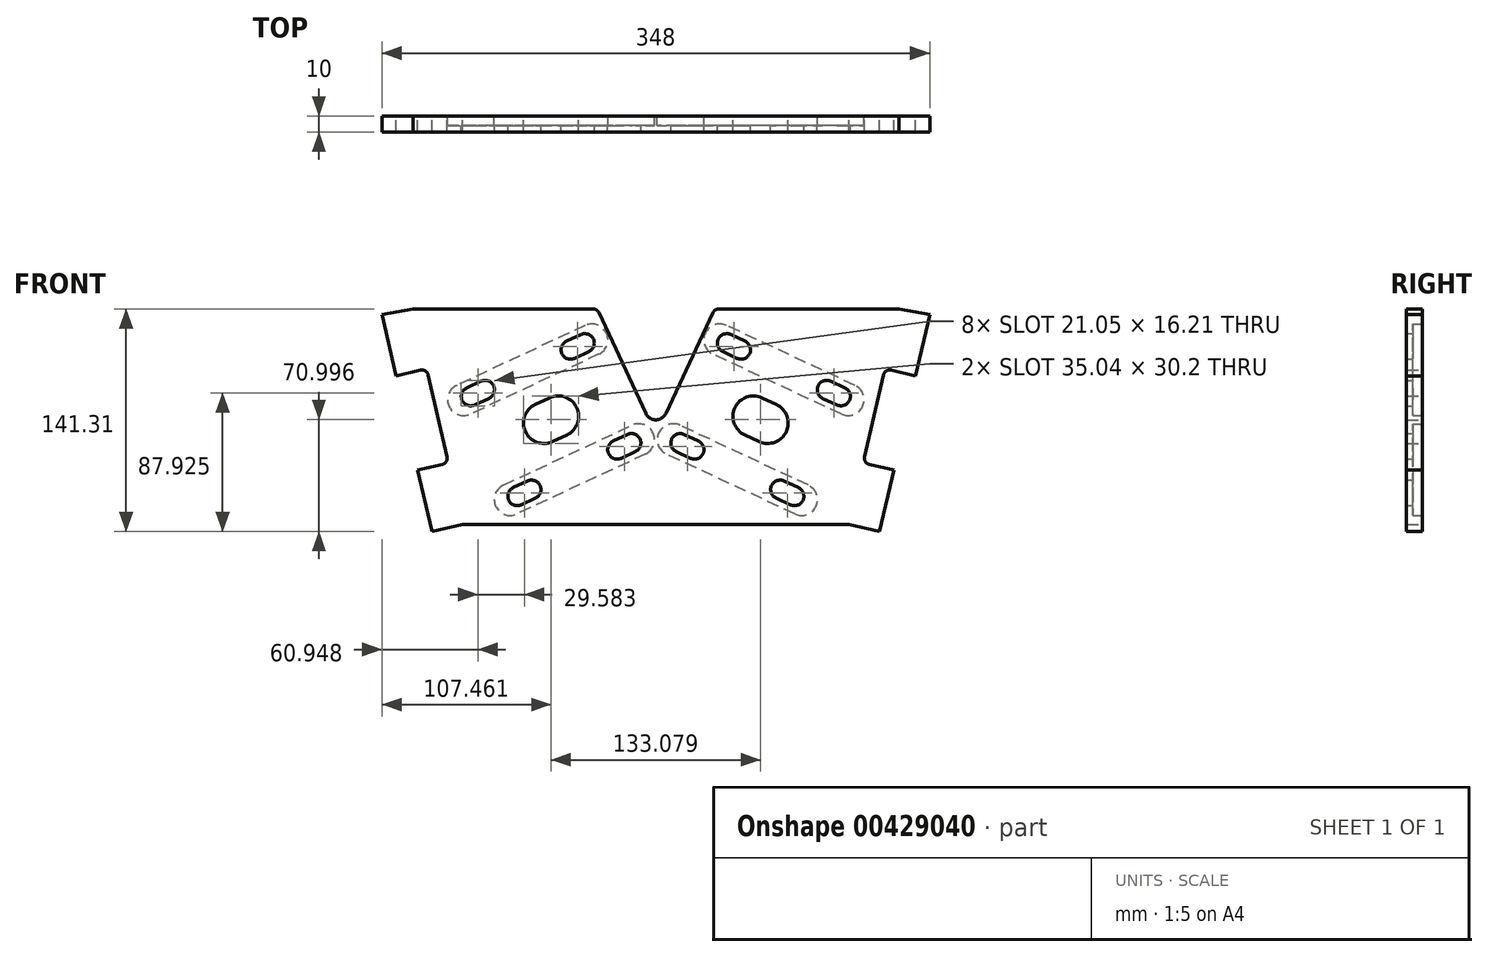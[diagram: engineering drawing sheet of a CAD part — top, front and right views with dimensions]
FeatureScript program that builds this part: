
annotation { "Feature Type Name" : "Feature", "Feature Type Description" : "" }
export const myFeature = defineFeature(function(context is Context, id is Id, definition is map)
    precondition{}
    {
        {
            var Q0;
            Q0=qCreatedBy(makeId("Front.planeOp"),FACE);
            var sketch = newSketch(context, id + "F0", { "sketchPlane" : qUnion([Q0])});
            skLineSegment(sketch, "E0", {"start": v(-39.85, 69.94) * mm, "end": v(-154.27, 69.94) * mm});
            skArc(sketch, "E1", {"start": v(-90.54, -43.56) * mm, "mid": v(-93.44, -51.54) * mm, "end": v(-85.46, -54.44) * mm});
            skArc(sketch, "E2", {"start": v(-76.4, -50.21) * mm, "mid": v(-73.5, -42.24) * mm, "end": v(-81.47, -39.34) * mm});
            skLineSegment(sketch, "E3", {"start": v(-90.54, -43.56) * mm, "end": v(-81.47, -39.34) * mm});
            skLineSegment(sketch, "E4", {"start": v(-85.46, -54.44) * mm, "end": v(-76.4, -50.21) * mm});
            skArc(sketch, "E5.MirrorCS", {"start": v(-22.02, -24.85) * mm, "mid": v(-30, -21.95) * mm, "end": v(-27.1, -13.98) * mm});
            skLineSegment(sketch, "E6.MirrorCS", {"start": v(-12.96, -20.63) * mm, "end": v(-22.02, -24.85) * mm});
            skLineSegment(sketch, "E7.MirrorCS", {"start": v(-18.03, -9.75) * mm, "end": v(-27.1, -13.98) * mm});
            skArc(sketch, "E8.MirrorCS", {"start": v(-18.03, -9.75) * mm, "mid": v(-10.06, -12.65) * mm, "end": v(-12.96, -20.63) * mm});
            skLineSegment(sketch, "E9", {"start": v(-92.27, -39.85) * mm, "end": v(-19.76, -6.04) * mm});
            skLineSegment(sketch, "E10", {"start": v(-83.73, -58.15) * mm, "end": v(-11.23, -24.34) * mm});
            skArc(sketch, "E11", {"start": v(-6.7, -22.23) * mm, "mid": v(-1.81, -8.8) * mm, "end": v(-15.23, -3.92) * mm});
            skLineSegment(sketch, "E12", {"start": v(-19.76, -6.04) * mm, "end": v(-15.23, -3.92) * mm});
            skLineSegment(sketch, "E13", {"start": v(-11.23, -24.34) * mm, "end": v(-6.7, -22.23) * mm});
            skArc(sketch, "E14.MirrorCS", {"start": v(-88.26, -60.27) * mm, "mid": v(-101.69, -55.38) * mm, "end": v(-96.8, -41.96) * mm});
            skLineSegment(sketch, "E15.MirrorCS", {"start": v(-92.27, -39.85) * mm, "end": v(-96.8, -41.96) * mm});
            skLineSegment(sketch, "E16.MirrorCS", {"start": v(-83.73, -58.15) * mm, "end": v(-88.26, -60.27) * mm});
            skLineSegment(sketch, "E17.MirrorCS", {"start": v(-113.31, 5.29) * mm, "end": v(-40.81, 39.1) * mm});
            skLineSegment(sketch, "E18.MirrorCS", {"start": v(-121.85, 23.6) * mm, "end": v(-49.35, 57.4) * mm});
            skArc(sketch, "E19.MirrorCS", {"start": v(-126.38, 21.48) * mm, "mid": v(-131.27, 8.06) * mm, "end": v(-117.85, 3.17) * mm});
            skLineSegment(sketch, "E20.MirrorCS", {"start": v(-113.31, 5.29) * mm, "end": v(-117.85, 3.17) * mm});
            skLineSegment(sketch, "E21.MirrorCS", {"start": v(-121.85, 23.6) * mm, "end": v(-126.38, 21.48) * mm});
            skLineSegment(sketch, "E22.MirrorCS", {"start": v(-40.81, 39.1) * mm, "end": v(-36.28, 41.21) * mm});
            skLineSegment(sketch, "E23.MirrorCS", {"start": v(-49.35, 57.4) * mm, "end": v(-44.82, 59.52) * mm});
            skArc(sketch, "E24.MirrorCS", {"start": v(-44.82, 59.52) * mm, "mid": v(-31.4, 54.63) * mm, "end": v(-36.28, 41.21) * mm});
            skLineSegment(sketch, "E25.MirrorCS", {"start": v(-115.05, 9) * mm, "end": v(-105.98, 13.23) * mm});
            skArc(sketch, "E26.MirrorCS", {"start": v(-111.06, 24.1) * mm, "mid": v(-103.08, 21.2) * mm, "end": v(-105.98, 13.23) * mm});
            skLineSegment(sketch, "E27.MirrorCS", {"start": v(-120.12, 19.88) * mm, "end": v(-111.06, 24.1) * mm});
            skArc(sketch, "E28.MirrorCS", {"start": v(-115.05, 9) * mm, "mid": v(-123.02, 11.9) * mm, "end": v(-120.12, 19.88) * mm});
            skArc(sketch, "E29.MirrorCS", {"start": v(-42.54, 42.81) * mm, "mid": v(-39.64, 50.79) * mm, "end": v(-47.61, 53.69) * mm});
            skLineSegment(sketch, "E30.MirrorCS", {"start": v(-47.61, 53.69) * mm, "end": v(-56.68, 49.46) * mm});
            skLineSegment(sketch, "E31.MirrorCS", {"start": v(-42.54, 42.81) * mm, "end": v(-51.6, 38.59) * mm});
            skArc(sketch, "E32.MirrorCS", {"start": v(-56.68, 49.46) * mm, "mid": v(-59.58, 41.49) * mm, "end": v(-51.6, 38.59) * mm});
            skArc(sketch, "E33", {"start": v(-76.56, 9.3) * mm, "mid": v(-82.85, -7.98) * mm, "end": v(-65.58, -14.27) * mm});
            skLineSegment(sketch, "E34", {"start": v(-76.56, 9.3) * mm, "end": v(-67.5, 13.52) * mm});
            skLineSegment(sketch, "E35", {"start": v(-65.58, -14.27) * mm, "end": v(-56.51, -10.04) * mm});
            skArc(sketch, "E36.trimOffspring", {"start": v(-56.51, -10.04) * mm, "mid": v(-50.23, 7.23) * mm, "end": v(-67.5, 13.52) * mm});
            skLineSegment(sketch, "E37", {"start": v(-174, 66.5) * mm, "end": v(-165, 27.53) * mm});
            skLineSegment(sketch, "E38", {"start": v(-144.61, 28.13) * mm, "end": v(-132.58, -24) * mm});
            skLineSegment(sketch, "E39", {"start": v(-154.27, 69.94) * mm, "end": v(-174, 66.5) * mm});
            skLineSegment(sketch, "E40", {"start": v(-165, 27.53) * mm, "end": v(-149.41, 31.13) * mm});
            skLineSegment(sketch, "E41", {"start": v(-151.17, -32.4) * mm, "end": v(-135.58, -28.8) * mm});
            skLineSegment(sketch, "E42", {"start": v(-142.17, -71.37) * mm, "end": v(-122.68, -66.87) * mm});
            skLineSegment(sketch, "E43.trimOffspring", {"start": v(-151.17, -32.4) * mm, "end": v(-142.17, -71.37) * mm});
            skLineSegment(sketch, "E44.MirrorCS", {"start": v(47.61, 53.69) * mm, "end": v(56.68, 49.46) * mm});
            skLineSegment(sketch, "E45.MirrorCS", {"start": v(83.73, -58.15) * mm, "end": v(88.26, -60.27) * mm});
            skLineSegment(sketch, "E46.MirrorCS", {"start": v(42.54, 42.81) * mm, "end": v(51.6, 38.59) * mm});
            skLineSegment(sketch, "E47.MirrorCS", {"start": v(121.85, 23.6) * mm, "end": v(126.38, 21.48) * mm});
            skLineSegment(sketch, "E48.MirrorCS", {"start": v(18.03, -9.75) * mm, "end": v(27.1, -13.98) * mm});
            skLineSegment(sketch, "E49.MirrorCS", {"start": v(113.31, 5.29) * mm, "end": v(117.85, 3.17) * mm});
            skLineSegment(sketch, "E50.MirrorCS", {"start": v(65.58, -14.27) * mm, "end": v(56.51, -10.04) * mm});
            skLineSegment(sketch, "E51.MirrorCS", {"start": v(85.46, -54.44) * mm, "end": v(76.4, -50.21) * mm});
            skLineSegment(sketch, "E52.MirrorCS", {"start": v(115.05, 9) * mm, "end": v(105.98, 13.23) * mm});
            skLineSegment(sketch, "E53.MirrorCS", {"start": v(12.96, -20.63) * mm, "end": v(22.02, -24.85) * mm});
            skLineSegment(sketch, "E54.MirrorCS", {"start": v(40.81, 39.1) * mm, "end": v(36.28, 41.21) * mm});
            skLineSegment(sketch, "E55.MirrorCS", {"start": v(11.23, -24.34) * mm, "end": v(6.7, -22.23) * mm});
            skLineSegment(sketch, "E56.MirrorCS", {"start": v(120.12, 19.88) * mm, "end": v(111.06, 24.1) * mm});
            skLineSegment(sketch, "E57.MirrorCS", {"start": v(76.56, 9.3) * mm, "end": v(67.5, 13.52) * mm});
            skLineSegment(sketch, "E58.MirrorCS", {"start": v(49.35, 57.4) * mm, "end": v(44.82, 59.52) * mm});
            skLineSegment(sketch, "E59.MirrorCS", {"start": v(90.54, -43.56) * mm, "end": v(81.47, -39.34) * mm});
            skLineSegment(sketch, "E60.MirrorCS", {"start": v(19.76, -6.04) * mm, "end": v(15.23, -3.92) * mm});
            skLineSegment(sketch, "E61.MirrorCS", {"start": v(92.27, -39.85) * mm, "end": v(96.8, -41.96) * mm});
            skArc(sketch, "E62.MirrorCS", {"start": v(42.54, 42.81) * mm, "mid": v(39.64, 50.79) * mm, "end": v(47.61, 53.69) * mm});
            skArc(sketch, "E63.MirrorCS", {"start": v(18.03, -9.75) * mm, "mid": v(10.06, -12.65) * mm, "end": v(12.96, -20.63) * mm});
            skLineSegment(sketch, "E64.MirrorCS", {"start": v(39.85, 69.94) * mm, "end": v(154.27, 69.94) * mm});
            skArc(sketch, "E65.MirrorCS", {"start": v(115.05, 9) * mm, "mid": v(123.02, 11.9) * mm, "end": v(120.12, 19.88) * mm});
            skArc(sketch, "E66.MirrorCS", {"start": v(90.54, -43.56) * mm, "mid": v(93.44, -51.54) * mm, "end": v(85.46, -54.44) * mm});
            skLineSegment(sketch, "E67.MirrorCS", {"start": v(92.27, -39.85) * mm, "end": v(19.76, -6.04) * mm});
            skArc(sketch, "E68.MirrorCS", {"start": v(44.82, 59.52) * mm, "mid": v(31.4, 54.63) * mm, "end": v(36.28, 41.21) * mm});
            skLineSegment(sketch, "E69.MirrorCS", {"start": v(174, 66.5) * mm, "end": v(165, 27.53) * mm});
            skLineSegment(sketch, "E70.MirrorCS", {"start": v(113.31, 5.29) * mm, "end": v(40.81, 39.1) * mm});
            skLineSegment(sketch, "E71.MirrorCS", {"start": v(83.73, -58.15) * mm, "end": v(11.23, -24.34) * mm});
            skLineSegment(sketch, "E72.MirrorCS", {"start": v(154.27, 69.94) * mm, "end": v(39.85, 69.94) * mm});
            skArc(sketch, "E73.MirrorCS", {"start": v(56.51, -10.04) * mm, "mid": v(50.23, 7.23) * mm, "end": v(67.5, 13.52) * mm});
            skLineSegment(sketch, "E74.MirrorCS", {"start": v(154.27, 69.94) * mm, "end": v(174, 66.5) * mm});
            skArc(sketch, "E75.MirrorCS", {"start": v(56.68, 49.46) * mm, "mid": v(59.58, 41.49) * mm, "end": v(51.6, 38.59) * mm});
            skArc(sketch, "E76.MirrorCS", {"start": v(6.7, -22.23) * mm, "mid": v(1.81, -8.8) * mm, "end": v(15.23, -3.92) * mm});
            skArc(sketch, "E77.MirrorCS", {"start": v(88.26, -60.27) * mm, "mid": v(101.69, -55.38) * mm, "end": v(96.8, -41.96) * mm});
            skArc(sketch, "E78.MirrorCS", {"start": v(22.02, -24.85) * mm, "mid": v(30, -21.95) * mm, "end": v(27.1, -13.98) * mm});
            skArc(sketch, "E79.MirrorCS", {"start": v(111.06, 24.1) * mm, "mid": v(103.08, 21.2) * mm, "end": v(105.98, 13.23) * mm});
            skLineSegment(sketch, "E80.MirrorCS", {"start": v(121.85, 23.6) * mm, "end": v(49.35, 57.4) * mm});
            skLineSegment(sketch, "E81.MirrorCS", {"start": v(144.61, 28.13) * mm, "end": v(132.58, -24) * mm});
            skLineSegment(sketch, "E82.MirrorCS", {"start": v(165, 27.53) * mm, "end": v(149.41, 31.13) * mm});
            skArc(sketch, "E83.MirrorCS", {"start": v(76.56, 9.3) * mm, "mid": v(82.85, -7.98) * mm, "end": v(65.58, -14.27) * mm});
            skLineSegment(sketch, "E84.MirrorCS", {"start": v(142.17, -71.37) * mm, "end": v(122.68, -66.87) * mm});
            skLineSegment(sketch, "E85.MirrorCS", {"start": v(151.17, -32.4) * mm, "end": v(135.58, -28.8) * mm});
            skArc(sketch, "E86.MirrorCS", {"start": v(76.4, -50.21) * mm, "mid": v(73.5, -42.24) * mm, "end": v(81.47, -39.34) * mm});
            skArc(sketch, "E87.MirrorCS", {"start": v(126.38, 21.48) * mm, "mid": v(131.27, 8.06) * mm, "end": v(117.85, 3.17) * mm});
            skLineSegment(sketch, "E88.MirrorCS", {"start": v(151.17, -32.4) * mm, "end": v(142.17, -71.37) * mm});
            skArc(sketch, "E89", {"start": v(-6.34, 3.55) * mm, "mid": v(0, -0.49) * mm, "end": v(6.34, 3.55) * mm});
            skLineSegment(sketch, "E90", {"start": v(6.34, 3.55) * mm, "end": v(36.22, 67.63) * mm});
            skLineSegment(sketch, "E91.MirrorCS", {"start": v(-6.34, 3.55) * mm, "end": v(-36.22, 67.63) * mm});
            skArc(sketch, "E92.filletArc", {"start": v(-36.22, 67.63) * mm, "mid": v(-37.7, 69.31) * mm, "end": v(-39.85, 69.94) * mm});
            skArc(sketch, "E93.filletArc", {"start": v(39.85, 69.94) * mm, "mid": v(37.7, 69.31) * mm, "end": v(36.22, 67.63) * mm});
            skLineSegment(sketch, "E94", {"start": v(-122.68, -66.87) * mm, "end": v(122.68, -66.87) * mm});
            skPoint(sketch, "E95.visualSharp", {"position": v(-145.51, 32.03) * mm});
            skArc(sketch, "E95.filletArc", {"start": v(-144.61, 28.13) * mm, "mid": v(-146.4, 30.62) * mm, "end": v(-149.41, 31.13) * mm});
            skPoint(sketch, "E96.visualSharp", {"position": v(-131.68, -27.9) * mm});
            skArc(sketch, "E96.filletArc", {"start": v(-135.58, -28.8) * mm, "mid": v(-133.09, -27.02) * mm, "end": v(-132.58, -24) * mm});
            skPoint(sketch, "E97.visualSharp", {"position": v(145.51, 32.03) * mm});
            skArc(sketch, "E97.filletArc", {"start": v(149.41, 31.13) * mm, "mid": v(146.4, 30.62) * mm, "end": v(144.61, 28.13) * mm});
            skPoint(sketch, "E98.visualSharp", {"position": v(131.68, -27.9) * mm});
            skArc(sketch, "E98.filletArc", {"start": v(132.58, -24) * mm, "mid": v(133.09, -27.02) * mm, "end": v(135.58, -28.8) * mm});
            skSolve(sketch);
        }
        {
            var Q0;
            Q0 = qSketchRegion(id + "F0", true);
            extrude(context, id + "F1", {"entities" : qUnion([Q0]), "depth" : 10 * mm});
        }
        {
            var Q0;
            Q0=makeQuery(id+"F0.imprint","IMPRINT",FACE,{"disambiguationData":[TD([[makeQuery(id+"F0.imprint","IMPRINT",EDGE,{"derivedFrom":sQuery(id+"F0.wireOp",EDGE,"E17.MirrorCS")}),1.0]])]});
            var Q1;
            Q1=makeQuery(id+"F0.imprint","IMPRINT",FACE,{"disambiguationData":[TD([[makeQuery(id+"F0.imprint","IMPRINT",EDGE,{"derivedFrom":sQuery(id+"F0.wireOp",EDGE,"E1")}),-1.0]])]});
            var Q2;
            Q2=makeQuery(id+"F0.imprint","IMPRINT",FACE,{"disambiguationData":[TD([[makeQuery(id+"F0.imprint","IMPRINT",EDGE,{"derivedFrom":sQuery(id+"F0.wireOp",EDGE,"E44.MirrorCS")}),1.0]])]});
            var Q3;
            Q3=makeQuery(id+"F0.imprint","IMPRINT",FACE,{"disambiguationData":[TD([[makeQuery(id+"F0.imprint","IMPRINT",EDGE,{"derivedFrom":sQuery(id+"F0.wireOp",EDGE,"E45.MirrorCS")}),1.0]])]});
            extrude(context, id + "F2", {"entities" : qUnion([Q0, Q1, Q2, Q3]), "operationType" : NewBodyOperationType.ADD, "depth" : 10 * mm, "hasSecondDirection" : true, "secondDirectionOppositeDirection" : true, "secondDirectionDepth" : -6.1 * mm});
        }
    });
